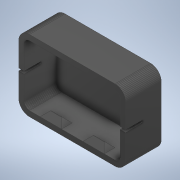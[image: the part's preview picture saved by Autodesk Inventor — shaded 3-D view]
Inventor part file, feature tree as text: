
AUTODESK INVENTOR PART (.ipt)
format: ipt  version: 2020 (Build 240168000, 168)  size: 264,192 bytes
history: native  units: in
note: dims shown in document units (in); Inventor stores cm internally (conversion verified against a paired STEP export)
features: other x3, extrude x2, sketch x2, direct_edit x1
ambient origin geometry x8: Origin, YZ Plane, XZ Plane, XY Plane, X Axis, Y Axis, Z Axis, Center Point
bodies: Solid1 (feature_tree)
feature tree (8):
  other  "ParametricSnapCaseAdaLikeBox-small-ZM20210904"
  other  "MeshFeature1"
  direct_edit  "Direct Edit1"
  extrude  "Extrusion1"  Depth=0.0709in
  extrude  "Extrusion2"  Depth=0.0709in
  sketch  "Sketch1"  dims[d0=0.0394in d1=0.3937in d2=0.3937in d3=0.0709in]
  sketch  "Sketch2"  dims[d4=0.0in d5=0.0in d6=0.0709in d7=0.0in d8=0.0in]
  other  "Scale1"
